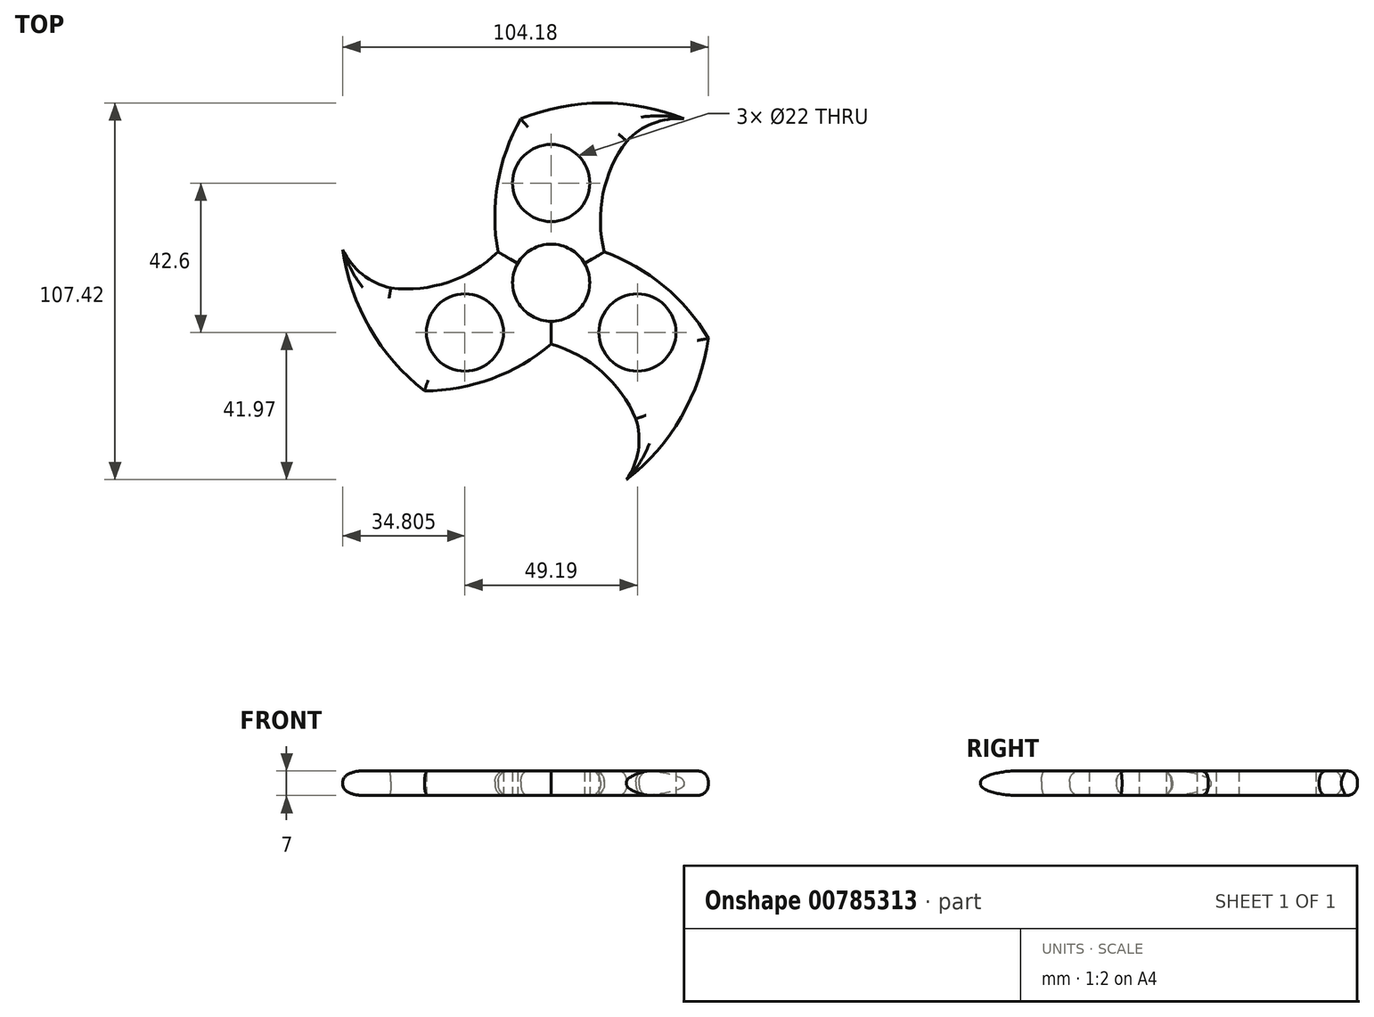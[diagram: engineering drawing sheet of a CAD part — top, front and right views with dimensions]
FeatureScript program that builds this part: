
annotation { "Feature Type Name" : "Feature", "Feature Type Description" : "" }
export const myFeature = defineFeature(function(context is Context, id is Id, definition is map)
    precondition{}
    {
        {
            var Q0;
            Q0=qCreatedBy(makeId("Top.planeOp"),FACE);
            var sketch = newSketch(context, id + "F0", { "sketchPlane" : qUnion([Q0])});
            skLineSegment(sketch, "E0", {"start": v(0, 0) * mm, "end": v(-9.53, 5.5) * mm});
            skLineSegment(sketch, "E1", {"start": v(0, 0) * mm, "end": v(9.53, 5.5) * mm});
            skArc(sketch, "E2", {"start": v(9.53, 5.5) * mm, "mid": v(0, 11) * mm, "end": v(-9.53, 5.5) * mm});
            skCircle(sketch, "E3", {"center": v(0, 28.4) * mm, "radius": 11 * mm});
            skLineSegment(sketch, "E4", {"start": v(-9.53, 5.5) * mm, "end": v(-15.16, 8.75) * mm});
            skLineSegment(sketch, "E5", {"start": v(9.53, 5.5) * mm, "end": v(15.16, 8.75) * mm});
            skArc(sketch, "E6", {"start": v(-8.65, 46.72) * mm, "mid": v(-15.24, 28.3) * mm, "end": v(-15.16, 8.75) * mm});
            skArc(sketch, "E7", {"start": v(37.89, 46.72) * mm, "mid": v(14.62, 51.25) * mm, "end": v(-8.65, 46.72) * mm});
            skArc(sketch, "E8", {"start": v(37.89, 46.72) * mm, "mid": v(28.98, 45.41) * mm, "end": v(21.54, 40.35) * mm});
            skArc(sketch, "E9", {"start": v(21.54, 40.35) * mm, "mid": v(14.78, 25.27) * mm, "end": v(15.16, 8.75) * mm});
            skSolve(sketch);
        }
        {
            var Q0;
            Q0=qCreatedBy(makeId("Front.planeOp"),FACE);
            var sketch = newSketch(context, id + "F1", { "sketchPlane" : qUnion([Q0])});
            skLineSegment(sketch, "E10", {"start": v(0, 0) * mm, "end": v(0, -12.8) * mm});
            skSolve(sketch);
        }
        {
            var Q0;
            Q0=makeQuery(id+"F0.imprint","IMPRINT",FACE,{"disambiguationData":[TD([[makeQuery(id+"F0.imprint","IMPRINT",EDGE,{"derivedFrom":sQuery(id+"F0.wireOp",EDGE,"E2")}),-1.0]])]});
            extrude(context, id + "F2", {"entities" : qUnion([Q0]), "depth" : 7 * mm, "offsetDistance" : 25 * mm});
        }
        {
            var Q0;
            Q0=makeQuery(id+"F2.opExtrude","CAP_EDGE",EDGE,{"disambiguationData":[OSD([sQuery(id+"F0.wireOp",EDGE,"E7")])],"isStart":true});
            var Q1;
            Q1=makeQuery(id+"F2.opExtrude","CAP_EDGE",EDGE,{"disambiguationData":[OSD([sQuery(id+"F0.wireOp",EDGE,"E7")])],"isStart":false});
            var Q2;
            Q2=makeQuery(id+"F2.opExtrude","CAP_EDGE",EDGE,{"disambiguationData":[OSD([sQuery(id+"F0.wireOp",EDGE,"E6")])],"isStart":true});
            var Q3;
            Q3=makeQuery(id+"F2.opExtrude","CAP_EDGE",EDGE,{"disambiguationData":[OSD([sQuery(id+"F0.wireOp",EDGE,"E6")])],"isStart":false});
            var Q4;
            Q4=makeQuery(id+"F2.opExtrude","CAP_EDGE",EDGE,{"disambiguationData":[OSD([sQuery(id+"F0.wireOp",EDGE,"E9")])],"isStart":false});
            var Q5;
            Q5=makeQuery(id+"F2.opExtrude","CAP_EDGE",EDGE,{"disambiguationData":[OSD([sQuery(id+"F0.wireOp",EDGE,"E8")])],"isStart":false});
            var Q6;
            Q6=makeQuery(id+"F2.opExtrude","CAP_EDGE",EDGE,{"disambiguationData":[OSD([sQuery(id+"F0.wireOp",EDGE,"E8")])],"isStart":true});
            var Q7;
            Q7=makeQuery(id+"F2.opExtrude","CAP_EDGE",EDGE,{"disambiguationData":[OSD([sQuery(id+"F0.wireOp",EDGE,"E9")])],"isStart":true});
            fillet(context, id + "F3", {"entities" : qUnion([Q0, Q1, Q2, Q3, Q4, Q5, Q6, Q7]), "radius" : 3 * mm, "tangentPropagation" : true, "allowEdgeOverflow" : false});
        }
        {
            var Q0;
            Q0=makeQuery(id+"F2.opExtrude","SWEPT_BODY",BODY,{"disambiguationData":[OSD([sQuery(id+"F0.wireOp",EDGE,"E2"),sQuery(id+"F0.wireOp",EDGE,"E3"),sQuery(id+"F0.wireOp",EDGE,"E4"),sQuery(id+"F0.wireOp",EDGE,"E5"),sQuery(id+"F0.wireOp",EDGE,"E6"),sQuery(id+"F0.wireOp",EDGE,"E7"),sQuery(id+"F0.wireOp",EDGE,"E8"),sQuery(id+"F0.wireOp",EDGE,"E9")])]});
            var Q1;
            Q1=sQuery(id+"F1.wireOp",EDGE,"E10");
            circularPattern(context, id + "F4", {"entities" : qUnion([Q0]), "axis" : qUnion([Q1]), "angle" : 360 * degree, "instanceCount" : 3, "equalSpace" : true});
        }
    });
